# Revit family: 0049110 Feilo Sylvania Lighting Fixture SYLVEO LED 8000LM WIDE 3K
name_source: partatom
category: Lighting Fixtures
revit_build: Autodesk Revit 2017 (Build: 20190507_1515(x64)
units: mm (PartAtom-declared; Revit-internal decimal feet)

## family parameters
Cut with Voids When Loaded = No
Host = Face
Light Source = No
Part Type = Normal
Room Calculation Point = No
Round Connector Dimension = Use Diameter
Shared = No

## types (1)
- 0049110 SYLVEO LED 8000LM WIDE 3K
    Apparent Load = 82 VA
    Assembly Code = D5020200
    AssetType = Fixed
    BracketExtrusionEnd = 19 mm
    BracketExtrusionStart = -19 mm
    BracketFold = 25 mm  [stored 0.082021 ft]
    BracketInnerWidth = 261 mm
    BracketThickness = 3 mm  [stored 0.00984252 ft]
    BracketWidth = 37 mm
    Calculate Coefficient of Utilization = No
    ClassificationName = Uniclass2015
    ClassificationValue = EF_70_80
    Cost = 0 $
    Default Elevation = 1219 mm
    Description = Exterior LED Floodlight, comes complete with a 1000mm cable and adjustable bracket, aluminium housing, clear glass diffuser, IP66, IK08, Class I, 3000K, Non-dimming, 8354lm, 82W, 103lm/W, 2400mA, CRI70, 52° beam angle, 50000hrs, (LxWxD) 66x290x333mm
    DimmingControlOptions = Non dimmable
    DocumentationLiterature = http://www.sylvania-lighting.com
    DurationUnit = hours
    ElectricShockClassification = Class I
    ExpectedLife = 50000
    HingeDia = 52 mm
    HingeHeight = 90 mm  [stored 0.295276 ft]
    IfcExportAs = IfcLightFixtureType
    IfcExportType = IfcLightFixtureType
    ImpactProtectionIndex = IK08
    IngressProtection = IP66
    InputNominalFrequency = 50 Hz
    InputVoltage = 100-240V~
    Keynote = 16500
    Lamp = LED
    LampColourRenderingIndex = 70
    LampColourTemperature = 3000 K
    LampMacAdamStep = 6
    LampNominalLuminous = 8354 lm
    LampsType = LED
    LightOutputRatio = 100
    LuminousEfficacy = 102.5 lm/W
    Manufacturer = Feilo Sylvania
    ManufacturerName = Feilo Sylvania
    Material = aluminium housing, glass diffuser
    Material_1_FEILO = Body-Sylvania-Sylveo-Aluminium
    Material_2_FEILO = Diffuser-Sylvania-Sylveo-Glow
    Material_3_FEILO = <By Category>
    Material_4_FEILO = <By Category>
    Model = SYLVEO LED 8000LM WIDE 3K
    ModelNumber = 0049110
    ModelReference = SYLVEO LED 8000LM WIDE 3K
    Name = SYLVEO LED 8000LM WIDE 3K
    NominalHeight = 333 mm  [stored 1.09252 ft]
    NominalLength = 290 mm  [stored 0.951444 ft]
    NominalWidth = 0 mm  [stored 0 ft]
    PowerConsumption = 81.5 W
    PowerFactor = 0
    TotalWidth = 290 mm  [stored 0.951444 ft]
    Type Image = <None>
    TypeBody_FEILO = Sylveo Medium Body : 0049110 SYLVEO LED 8000LM WIDE 3K
    TypeName = SYLVEO LED 8000LM WIDE 3K
    URL = http://www.sylvania-lighting.com
    Voltage = 230 V
    Weight = 9.082 kg

note: [stored X ft] marks values corroborated as IEEE doubles in the binary element streams (Revit-internal decimal feet)

## geometry (parser evidence)
native form markers: Sweep x2
no freeform markers — native parametric forms only
